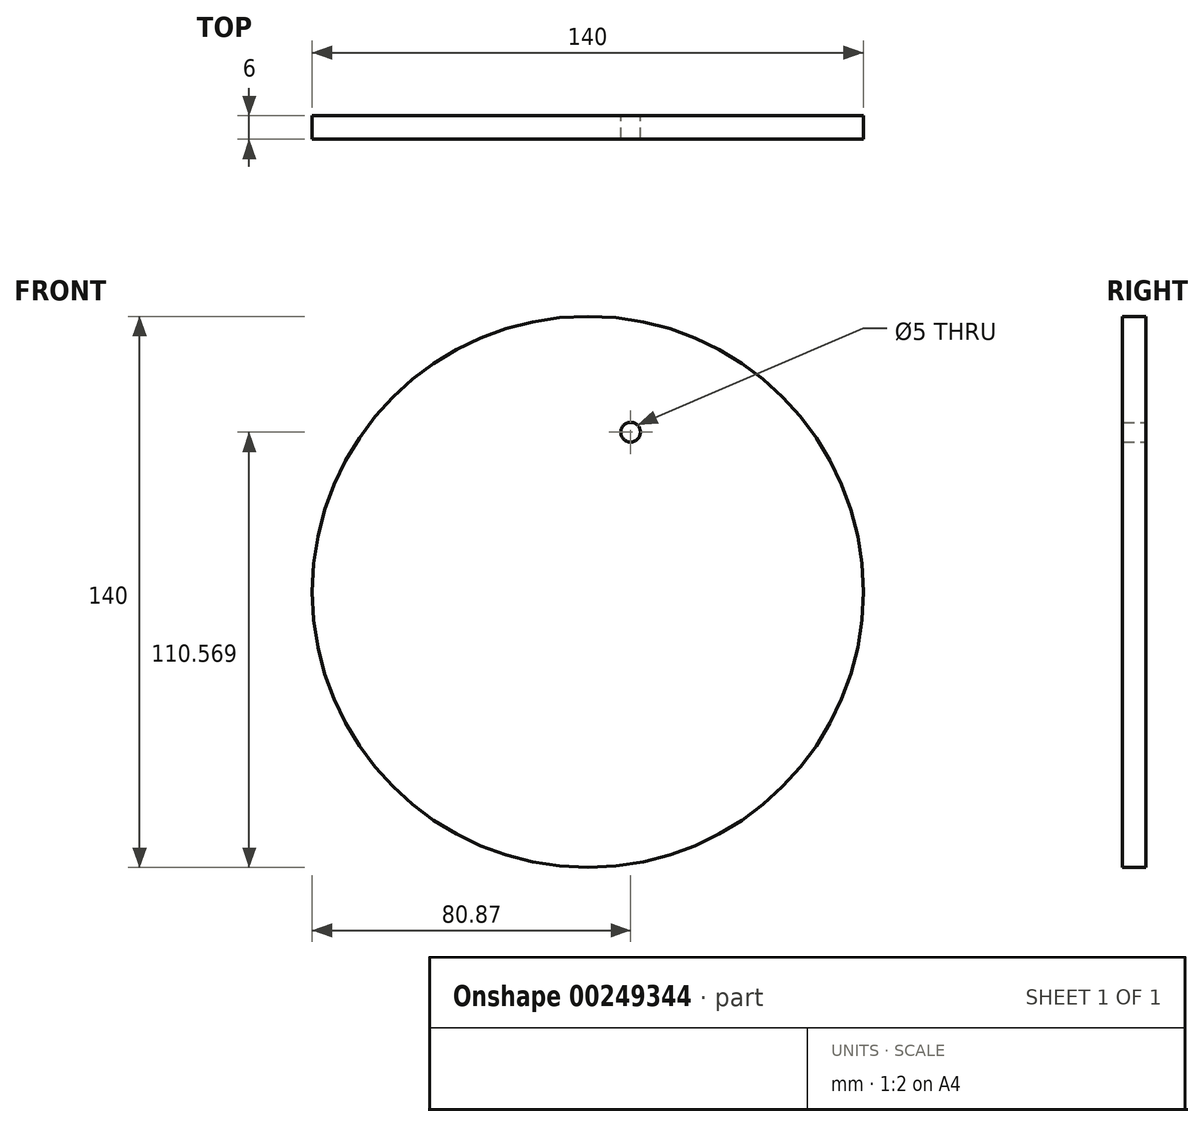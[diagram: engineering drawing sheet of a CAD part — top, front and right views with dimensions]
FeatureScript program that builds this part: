
annotation { "Feature Type Name" : "Feature", "Feature Type Description" : "" }
export const myFeature = defineFeature(function(context is Context, id is Id, definition is map)
    precondition{}
    {
        {
            var Q0;
            Q0=qCreatedBy(makeId("Front.planeOp"),FACE);
            var sketch = newSketch(context, id + "F0", { "sketchPlane" : qUnion([Q0])});
            skCircle(sketch, "E0", {"center": v(0, 0) * mm, "radius": 70 * mm});
            skSolve(sketch);
        }
        {
            var Q0;
            Q0=makeQuery(id+"F0.imprint","IMPRINT",FACE,{"disambiguationData":[TD([[makeQuery(id+"F0.imprint","IMPRINT",EDGE,{"derivedFrom":sQuery(id+"F0.wireOp",EDGE,"E0")}),1.0]])]});
            extrude(context, id + "F1", {"entities" : qUnion([Q0]), "depth" : 6 * mm, "symmetric" : true});
        }
        {
            var Q0;
            Q0=qCreatedBy(makeId("Front.planeOp"),FACE);
            var sketch = newSketch(context, id + "F2", { "sketchPlane" : qUnion([Q0])});
            skCircle(sketch, "E1", {"center": v(10.87, 40.57) * mm, "radius": 2.5 * mm});
            skLineSegment(sketch, "E2", {"start": v(10.87, 40.57) * mm, "end": v(0, 0) * mm, "construction": true});
            skSolve(sketch);
        }
        {
            var Q0;
            Q0=makeQuery(id+"F2.imprint","IMPRINT",FACE,{"disambiguationData":[TD([[makeQuery(id+"F2.imprint","IMPRINT",EDGE,{"derivedFrom":sQuery(id+"F2.wireOp",EDGE,"E1")}),1.0]])]});
            extrude(context, id + "F3", {"entities" : qUnion([Q0]), "operationType" : NewBodyOperationType.REMOVE, "depth" : 25 * mm, "symmetric" : true});
        }
    });
